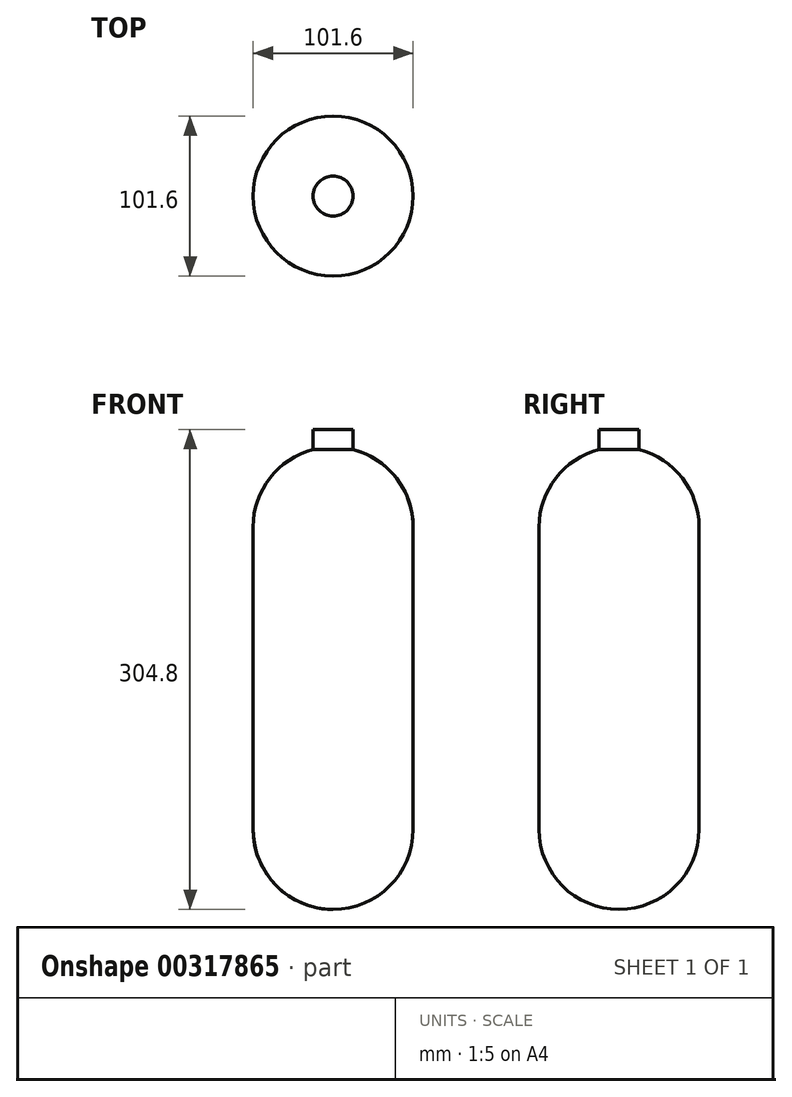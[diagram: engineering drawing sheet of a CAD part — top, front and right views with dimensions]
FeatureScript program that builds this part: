
annotation { "Feature Type Name" : "Feature", "Feature Type Description" : "" }
export const myFeature = defineFeature(function(context is Context, id is Id, definition is map)
    precondition{}
    {
        {
            var Q0;
            Q0=qCreatedBy(makeId("Front.planeOp"),FACE);
            var sketch = newSketch(context, id + "F0", { "sketchPlane" : qUnion([Q0])});
            skLineSegment(sketch, "E0", {"start": v(0, 152.4) * mm, "end": v(0, -152.4) * mm});
            skArc(sketch, "E1", {"start": v(0, -152.4) * mm, "mid": v(35.92, -137.52) * mm, "end": v(50.8, -101.6) * mm});
            skLineSegment(sketch, "E2", {"start": v(50.8, -101.6) * mm, "end": v(50.8, 90.51) * mm});
            skArc(sketch, "E3", {"start": v(50.8, 90.51) * mm, "mid": v(40.16, 121.62) * mm, "end": v(12.7, 139.7) * mm});
            skLineSegment(sketch, "E4", {"start": v(12.7, 139.7) * mm, "end": v(12.7, 152.4) * mm});
            skLineSegment(sketch, "E5", {"start": v(12.7, 152.4) * mm, "end": v(0, 152.4) * mm});
            skSolve(sketch);
        }
        {
            var Q0;
            Q0=makeQuery(id+"F0.imprint","IMPRINT",FACE,{"disambiguationData":[TD([[makeQuery(id+"F0.imprint","IMPRINT",EDGE,{"derivedFrom":sQuery(id+"F0.wireOp",EDGE,"E0")}),1.0]])]});
            var Q1;
            Q1=sQuery(id+"F0.wireOp",EDGE,"E0");
            revolve(context, id + "F1", {"entities" : qUnion([Q0]), "axis" : qUnion([Q1]), "revolveType" : RevolveType.FULL});
        }
    });
